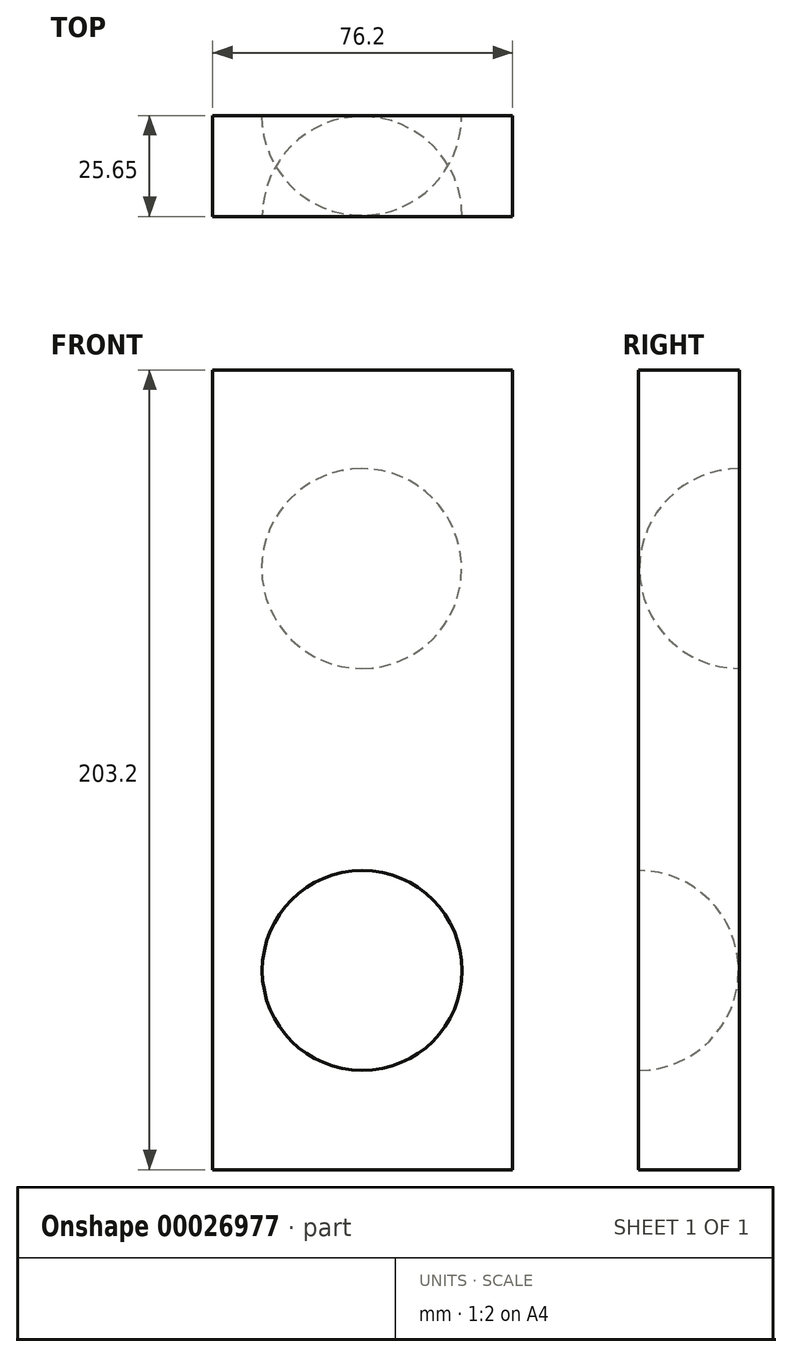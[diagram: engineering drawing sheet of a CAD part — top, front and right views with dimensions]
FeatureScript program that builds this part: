
annotation { "Feature Type Name" : "Feature", "Feature Type Description" : "" }
export const myFeature = defineFeature(function(context is Context, id is Id, definition is map)
    precondition{}
    {
        {
            var Q0;
            Q0=qCreatedBy(makeId("Front.planeOp"),FACE);
            var sketch = newSketch(context, id + "F0", { "sketchPlane" : qUnion([Q0])});
            skLineSegment(sketch, "E0.bottom", {"start": v(32.6, -94.42) * mm, "end": v(-43.6, -94.42) * mm});
            skLineSegment(sketch, "E0.top", {"start": v(32.6, 108.78) * mm, "end": v(-43.6, 108.78) * mm});
            skLineSegment(sketch, "E0.left", {"start": v(32.6, -94.42) * mm, "end": v(32.6, 108.78) * mm});
            skLineSegment(sketch, "E0.right", {"start": v(-43.6, -94.42) * mm, "end": v(-43.6, 108.78) * mm});
            skLineSegment(sketch, "E1", {"start": v(-5.5, -18.22) * mm, "end": v(-5.5, -69.02) * mm});
            skArc(sketch, "E2", {"start": v(-5.5, -69.02) * mm, "mid": v(19.9, -43.62) * mm, "end": v(-5.5, -18.22) * mm});
            skPoint(sketch, "E3.orphan", {"position": v(-5.5, 7.18) * mm});
            skPoint(sketch, "E4.trimOffspring.end.orphan", {"position": v(32.6, -43.62) * mm});
            skPoint(sketch, "E5.start.orphan", {"position": v(-43.6, -43.62) * mm});
            skPoint(sketch, "E6.orphan", {"position": v(-5.5, -94.42) * mm});
            skLineSegment(sketch, "E7", {"start": v(-5.5, 32.74) * mm, "end": v(-5.5, 83.21) * mm});
            skArc(sketch, "E8", {"start": v(-5.5, 32.74) * mm, "mid": v(19.74, 57.98) * mm, "end": v(-5.5, 83.21) * mm});
            skPoint(sketch, "E9.orphan", {"position": v(-5.5, 108.78) * mm});
            skPoint(sketch, "E10.orphan", {"position": v(-43.6, 57.98) * mm});
            skPoint(sketch, "E11.end.orphan", {"position": v(32.6, 57.98) * mm});
            skPoint(sketch, "E12.orphan", {"position": v(32.6, 108.78) * mm});
            skPoint(sketch, "E13.orphan", {"position": v(-43.6, 7.18) * mm});
            skPoint(sketch, "E14.orphan", {"position": v(-43.6, -94.42) * mm});
            skPoint(sketch, "E15.left.end.orphan", {"position": v(32.6, 7.18) * mm});
            skSolve(sketch);
        }
        {
            var Q0;
            Q0=qSketchRegion(id+"F0",true);
            var Q1;
            Q1=makeQuery(id+"F0.imprint","IMPRINT",FACE,{"disambiguationData":[TD([[makeQuery(id+"F0.imprint","IMPRINT",EDGE,{"derivedFrom":sQuery(id+"F0.wireOp",EDGE,"E7")}),-1.0]])]});
            var Q2;
            Q2=makeQuery(id+"F0.imprint","IMPRINT",FACE,{"disambiguationData":[TD([[makeQuery(id+"F0.imprint","IMPRINT",EDGE,{"derivedFrom":sQuery(id+"F0.wireOp",EDGE,"E1")}),1.0]])]});
            extrude(context, id + "F1", {"entities" : qUnion([Q0, Q1, Q2]), "oppositeDirection" : true, "depth" : 25.65 * mm});
        }
        {
            var Q0;
            Q0=qCreatedBy(makeId("Front.planeOp"),FACE);
            var sketch = newSketch(context, id + "F2", { "sketchPlane" : qUnion([Q0])});
            skLineSegment(sketch, "E16", {"start": v(-5.6, -18.42) * mm, "end": v(-5.6, -69.22) * mm});
            skArc(sketch, "E17", {"start": v(-5.6, -69.22) * mm, "mid": v(19.8, -43.82) * mm, "end": v(-5.6, -18.42) * mm});
            skLineSegment(sketch, "E18", {"start": v(-5.55, 83.8) * mm, "end": v(-5.55, 33) * mm});
            skArc(sketch, "E19", {"start": v(-5.55, 33) * mm, "mid": v(19.85, 58.4) * mm, "end": v(-5.55, 83.8) * mm});
            skSolve(sketch);
        }
        {
            var Q0;
            Q0=makeQuery(id+"F2.imprint","IMPRINT",FACE,{"disambiguationData":[TD([[makeQuery(id+"F2.imprint","IMPRINT",EDGE,{"derivedFrom":sQuery(id+"F2.wireOp",EDGE,"E16")}),1.0]])]});
            var Q1;
            Q1=sQuery(id+"F2.wireOp",EDGE,"E16");
            revolve(context, id + "F3", {"operationType" : NewBodyOperationType.REMOVE, "entities" : qUnion([Q0]), "axis" : qUnion([Q1]), "revolveType" : RevolveType.FULL, "oppositeDirection" : true});
        }
        {
            var Q0;
            Q0=qCreatedBy(makeId("Front.planeOp"),FACE);
            cPlane(context, id + "F4", {"entities" : qUnion([Q0]), "cplaneType" : CPlaneType.OFFSET, "offset" : 25.65 * mm, "oppositeDirection" : true, "width" : 152.4 * mm, "height" : 152.4 * mm});
        }
        {
            var Q0;
            Q0=qCreatedBy(id+"F4.planeOp",FACE);
            var sketch = newSketch(context, id + "F5", { "sketchPlane" : qUnion([Q0])});
            skLineSegment(sketch, "E20", {"start": v(-5.74, 83.7) * mm, "end": v(-5.74, 32.9) * mm});
            skArc(sketch, "E21", {"start": v(-5.74, 83.7) * mm, "mid": v(-31.14, 58.3) * mm, "end": v(-5.74, 32.9) * mm});
            skSolve(sketch);
        }
        {
            var Q0;
            Q0 = qSketchRegion(id + "F5", true);
            var Q1;
            Q1=sQuery(id+"F5.wireOp",EDGE,"E20");
            revolve(context, id + "F6", {"operationType" : NewBodyOperationType.REMOVE, "entities" : qUnion([Q0]), "axis" : qUnion([Q1]), "revolveType" : RevolveType.ONE_DIRECTION, "oppositeDirection" : true, "angle" : 180 * degree});
        }
    });
